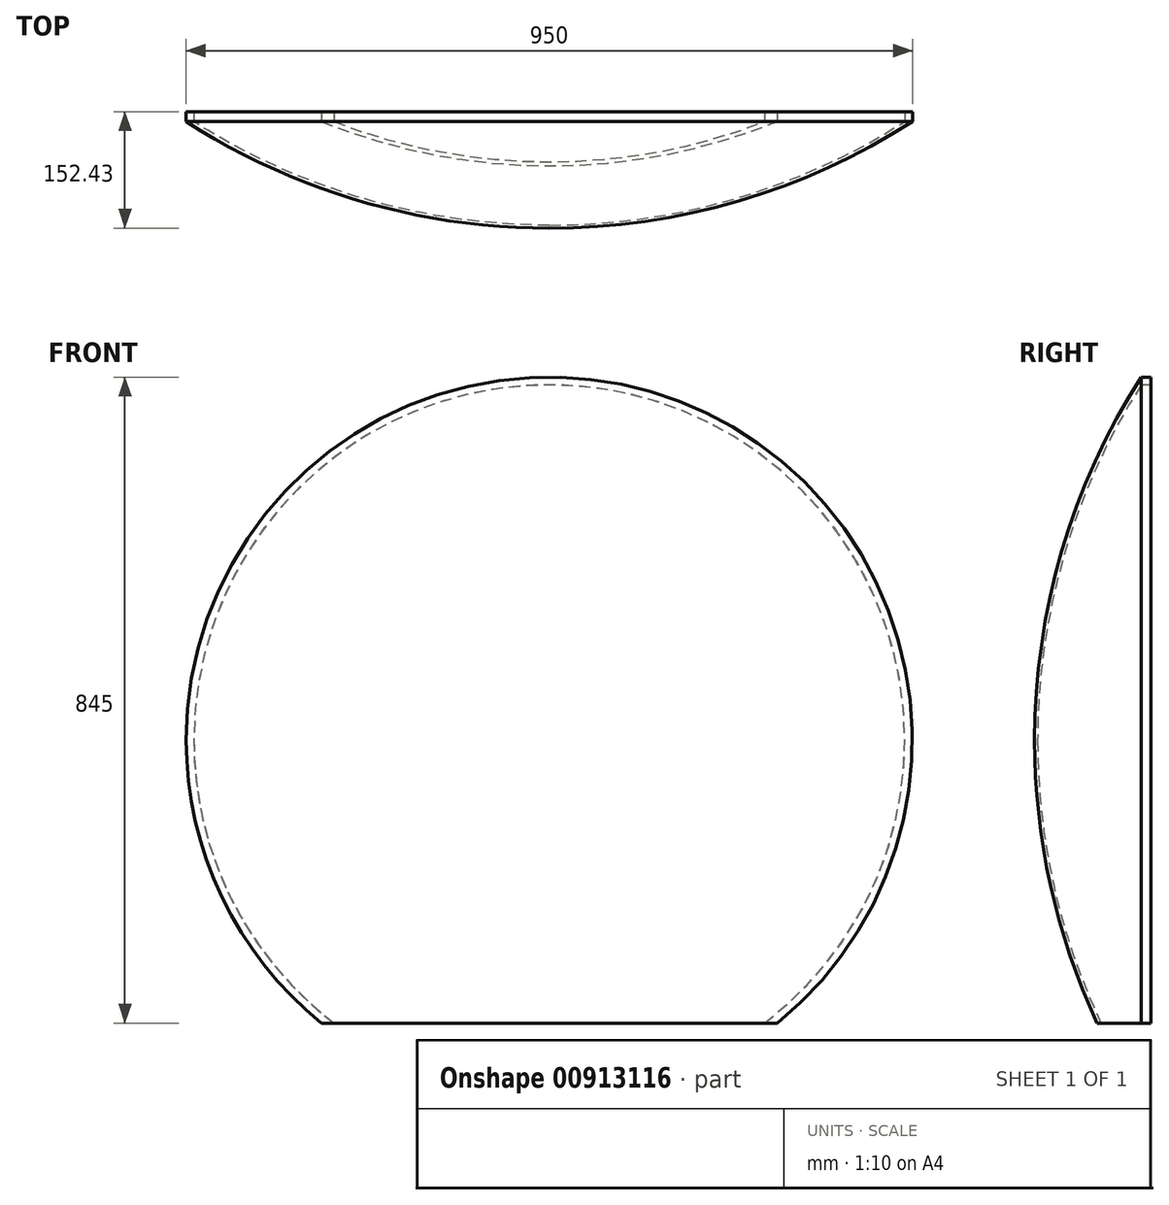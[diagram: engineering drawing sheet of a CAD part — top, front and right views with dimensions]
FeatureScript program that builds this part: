
annotation { "Feature Type Name" : "Feature", "Feature Type Description" : "" }
export const myFeature = defineFeature(function(context is Context, id is Id, definition is map)
    precondition{}
    {
        {
            var Q0;
            Q0=qCreatedBy(makeId("Front.planeOp"),FACE);
            var sketch = newSketch(context, id + "F0", { "sketchPlane" : qUnion([Q0])});
            skArc(sketch, "E0", {"start": v(475, 0) * mm, "mid": v(0, 475) * mm, "end": v(-475, 0) * mm});
            skPoint(sketch, "E1.start.orphan", {"position": v(-506.79, 0) * mm});
            skArc(sketch, "E2", {"start": v(-465, 0) * mm, "mid": v(0, 465) * mm, "end": v(465, 0) * mm});
            skLineSegment(sketch, "E3", {"start": v(-475, 0) * mm, "end": v(-465, 0) * mm});
            skLineSegment(sketch, "E4", {"start": v(465, 0) * mm, "end": v(475, 0) * mm});
            skSolve(sketch);
        }
        {
            var Q0;
            Q0=qCreatedBy(makeId("Right.planeOp"),FACE);
            var sketch = newSketch(context, id + "F1", { "sketchPlane" : qUnion([Q0])});
            skLineSegment(sketch, "E5", {"start": v(0, 0) * mm, "end": v(740, 0) * mm, "construction": true});
            skPoint(sketch, "E6", {"position": v(730, 0) * mm});
            skArc(sketch, "E7", {"start": v(0, 475) * mm, "mid": v(-103.78, 247.5) * mm, "end": v(-139.33, 0) * mm});
            skArc(sketch, "E8", {"start": v(0, 465) * mm, "mid": v(-100.95, 242.17) * mm, "end": v(-135.52, 0) * mm});
            skLineSegment(sketch, "E9", {"start": v(0, 465) * mm, "end": v(0, 475) * mm});
            skLineSegment(sketch, "E10", {"start": v(-135.52, 0) * mm, "end": v(-139.33, 0) * mm});
            skSolve(sketch);
        }
        {
            var Q0;
            Q0=makeQuery(id+"F0.imprint","IMPRINT",FACE,{"disambiguationData":[TD([[makeQuery(id+"F0.imprint","IMPRINT",EDGE,{"derivedFrom":sQuery(id+"F0.wireOp",EDGE,"E0")}),1.0]])]});
            extrude(context, id + "F2", {"entities" : qUnion([Q0]), "oppositeDirection" : true, "depth" : 13.1 * mm, "offsetDistance" : 25 * mm});
        }
        {
            var Q0;
            Q0=makeQuery(id+"F1.imprint","IMPRINT",FACE,{"disambiguationData":[TD([[makeQuery(id+"F1.imprint","IMPRINT",EDGE,{"derivedFrom":sQuery(id+"F1.wireOp",EDGE,"E7")}),1.0]])]});
            var Q1;
            Q1=sQuery(id+"F1.wireOp",EDGE,"E10");
            revolve(context, id + "F3", {"operationType" : NewBodyOperationType.ADD, "surfaceOperationType" : NewSurfaceOperationType.NEW, "entities" : qUnion([Q0]), "axis" : qUnion([Q1]), "revolveType" : RevolveType.SYMMETRIC, "angle" : 180 * degree});
        }
        {
            var Q0;
            Q0=makeQuery(id+"F2.opExtrude","SWEPT_BODY",BODY,{"disambiguationData":[OSD([sQuery(id+"F0.wireOp",EDGE,"E0"),sQuery(id+"F0.wireOp",EDGE,"E2"),sQuery(id+"F0.wireOp",EDGE,"E3"),sQuery(id+"F0.wireOp",EDGE,"E4")])]});
            var Q1;
            Q1=makeQuery(id+"F3.boolean.opBoolean","MERGE",FACE,{"derivedFrom":[makeQuery(id+"F2.opExtrude","SWEPT_FACE",FACE,{"disambiguationData":[OSD([sQuery(id+"F0.wireOp",EDGE,"E3")])]}),makeQuery(id+"F2.opExtrude","SWEPT_FACE",FACE,{"disambiguationData":[OSD([sQuery(id+"F0.wireOp",EDGE,"E4")])]}),makeQuery(id+"F3.opRevolve","CAP_FACE",FACE,{"disambiguationData":[OSD([sQuery(id+"F1.wireOp",EDGE,"E7"),sQuery(id+"F1.wireOp",EDGE,"E8"),sQuery(id+"F1.wireOp",EDGE,"E9"),sQuery(id+"F1.wireOp",EDGE,"E10")])],"isStart":true})]});
            mirror(context, id + "F4", {"operationType" : NewBodyOperationType.ADD, "entities" : qUnion([Q0]), "mirrorPlane" : qUnion([Q1])});
        }
        {
            var Q0;
            {var subQ0=makeQuery(id+"F2.opExtrude","CAP_FACE",FACE,{"disambiguationData":[OSD([sQuery(id+"F0.wireOp",EDGE,"E0"),sQuery(id+"F0.wireOp",EDGE,"E2"),sQuery(id+"F0.wireOp",EDGE,"E3"),sQuery(id+"F0.wireOp",EDGE,"E4")])],"isStart":false});Q0=makeQuery(id+"F4.boolean.opBoolean","MERGE",FACE,{"derivedFrom":[subQ0,makeQuery(id+"F4.opPattern","COPY",FACE,{"derivedFrom":subQ0,"instanceName":"1"})]});}
            var sketch = newSketch(context, id + "F5", { "sketchPlane" : qUnion([Q0])});
            skLineSegment(sketch, "E11", {"start": v(0, 475) * mm, "end": v(0, -370) * mm, "construction": true});
            skLineSegment(sketch, "E12.bottom", {"start": v(-331.62, -370) * mm, "end": v(340.46, -370) * mm});
            skLineSegment(sketch, "E12.top", {"start": v(-331.62, -490.8) * mm, "end": v(340.46, -490.8) * mm});
            skLineSegment(sketch, "E12.left", {"start": v(-331.62, -370) * mm, "end": v(-331.62, -490.8) * mm});
            skLineSegment(sketch, "E12.right", {"start": v(340.46, -370) * mm, "end": v(340.46, -490.8) * mm});
            skSolve(sketch);
        }
        {
            var Q0;
            Q0 = qSketchRegion(id + "F5", true);
            extrude(context, id + "F6", {"entities" : qUnion([Q0]), "operationType" : NewBodyOperationType.REMOVE, "oppositeDirection" : true, "depth" : 89 * mm, "offsetDistance" : 25 * mm});
        }
    });
